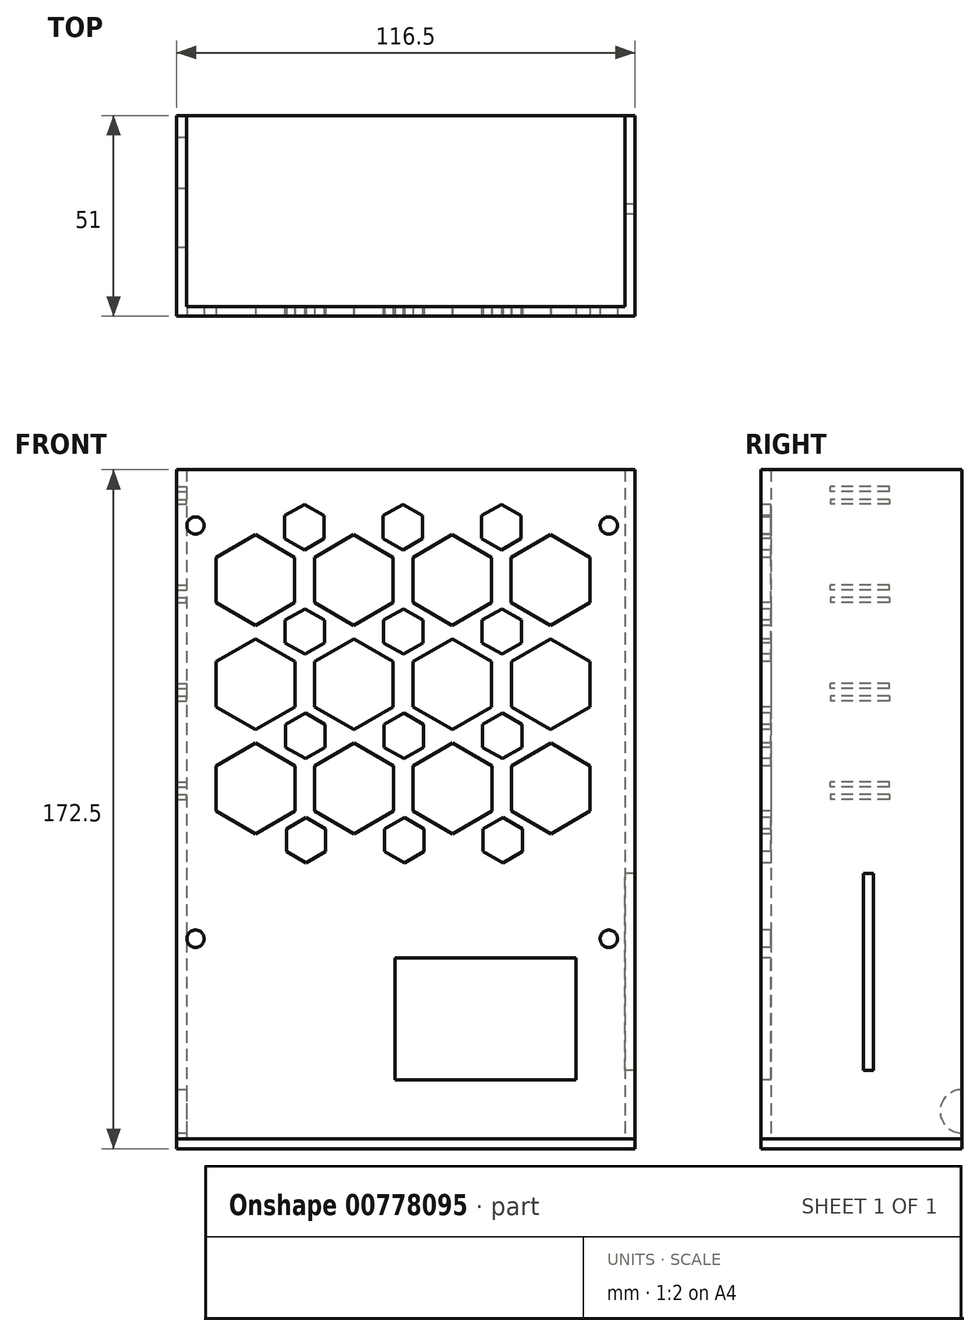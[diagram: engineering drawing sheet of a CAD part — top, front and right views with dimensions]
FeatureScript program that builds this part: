
annotation { "Feature Type Name" : "Feature", "Feature Type Description" : "" }
export const myFeature = defineFeature(function(context is Context, id is Id, definition is map)
    precondition{}
    {
        {
            var Q0;
            Q0=qCreatedBy(makeId("Top.planeOp"),FACE);
            var sketch = newSketch(context, id + "F0", { "sketchPlane" : qUnion([Q0])});
            skLineSegment(sketch, "E0", {"start": v(-38.54, 0) * mm, "end": v(77.96, 0) * mm});
            skLineSegment(sketch, "E1", {"start": v(-38.54, 0) * mm, "end": v(-38.54, 51) * mm});
            skLineSegment(sketch, "E2", {"start": v(77.96, 0) * mm, "end": v(77.96, 51) * mm});
            skLineSegment(sketch, "E3", {"start": v(-38.54, 51) * mm, "end": v(-36.04, 51) * mm});
            skLineSegment(sketch, "E4", {"start": v(-36.04, 51) * mm, "end": v(-36.04, 2.48) * mm});
            skLineSegment(sketch, "E5", {"start": v(-36.04, 2.48) * mm, "end": v(75.46, 2.48) * mm});
            skLineSegment(sketch, "E6", {"start": v(75.46, 2.48) * mm, "end": v(75.46, 51) * mm});
            skLineSegment(sketch, "E7", {"start": v(75.46, 51) * mm, "end": v(77.96, 51) * mm});
            skSolve(sketch);
        }
        {
            var Q0;
            Q0 = qSketchRegion(id + "F0", true);
            var Q1;
            Q1 = qSketchRegion(id + "F2", true);
            extrude(context, id + "F1", {"entities" : qUnion([Q0, Q1]), "depth" : 170 * mm, "offsetDistance" : 25.4 * mm});
        }
        {
            var Q0;
            Q0=qCreatedBy(makeId("Front.planeOp"),FACE);
            var sketch = newSketch(context, id + "F2", { "sketchPlane" : qUnion([Q0])});
            skLineSegment(sketch, "E8", {"start": v(-38.54, 0) * mm, "end": v(-38.54, -2.5) * mm});
            skLineSegment(sketch, "E9", {"start": v(-38.54, -2.5) * mm, "end": v(77.96, -2.5) * mm});
            skLineSegment(sketch, "E10", {"start": v(77.96, -2.5) * mm, "end": v(77.96, 0) * mm});
            skLineSegment(sketch, "E11", {"start": v(77.96, 0) * mm, "end": v(-38.54, 0) * mm});
            skSolve(sketch);
        }
        {
            var Q0;
            Q0 = qSketchRegion(id + "F2", true);
            extrude(context, id + "F3", {"entities" : qUnion([Q0]), "depth" : -51 * mm, "offsetDistance" : 25 * mm});
        }
        {
            var Q0;
            Q0=qCreatedBy(makeId("Front.planeOp"),FACE);
            var sketch = newSketch(context, id + "F4", { "sketchPlane" : qUnion([Q0])});
            skLineSegment(sketch, "E12.bottom", {"start": v(16.96, 46) * mm, "end": v(62.96, 46) * mm});
            skLineSegment(sketch, "E12.top", {"start": v(16.96, 15) * mm, "end": v(62.96, 15) * mm});
            skLineSegment(sketch, "E12.left", {"start": v(16.96, 46) * mm, "end": v(16.96, 15) * mm});
            skLineSegment(sketch, "E12.right", {"start": v(62.96, 46) * mm, "end": v(62.96, 15) * mm});
            skPoint(sketch, "E13", {"position": v(16.96, 0) * mm});
            skPoint(sketch, "E14", {"position": v(77.96, 15) * mm});
            skSolve(sketch);
        }
        {
            var Q0;
            Q0=makeQuery(id+"F4.imprint","IMPRINT",FACE,{"disambiguationData":[TD([[makeQuery(id+"F4.imprint","IMPRINT",EDGE,{"derivedFrom":sQuery(id+"F4.wireOp",EDGE,"E12.bottom")}),-1.0]])]});
            var Q1;
            Q1 = qSketchRegion(id + "F4", true);
            extrude(context, id + "F5", {"entities" : qUnion([Q0, Q1]), "operationType" : NewBodyOperationType.REMOVE, "depth" : -10 * mm, "offsetDistance" : 25 * mm});
        }
        {
            var Q0;
            Q0=qCreatedBy(makeId("Front.planeOp"),FACE);
            var sketch = newSketch(context, id + "F6", { "sketchPlane" : qUnion([Q0])});
            skLineSegment(sketch, "E15.left", {"start": v(-28.54, 180) * mm, "end": v(-28.54, 70) * mm});
            skLineSegment(sketch, "E15.right", {"start": v(67.96, 180) * mm, "end": v(67.96, 70) * mm});
            skCircle(sketch, "E16.1.0.0", {"center": v(31.5, 141.97) * mm, "radius": 11.55 * mm, "construction": true});
            skCircle(sketch, "E16.1.0.1", {"center": v(6.5, 141.97) * mm, "radius": 6.55 * mm, "construction": true});
            skLineSegment(sketch, "E16.1.0.2", {"start": v(50.83, 138.7) * mm, "end": v(50.83, 145.25) * mm});
            skLineSegment(sketch, "E16.1.0.3", {"start": v(-28.5, 136.2) * mm, "end": v(-28.5, 147.75) * mm});
            skLineSegment(sketch, "E16.1.0.4", {"start": v(-24.17, 138.7) * mm, "end": v(-24.17, 145.25) * mm});
            skLineSegment(sketch, "E16.1.0.5", {"start": v(-3.5, 136.2) * mm, "end": v(-3.5, 147.75) * mm});
            skLineSegment(sketch, "E16.1.0.6", {"start": v(46.5, 147.75) * mm, "end": v(56.5, 153.52) * mm});
            skLineSegment(sketch, "E16.1.0.7", {"start": v(16.5, 147.75) * mm, "end": v(16.5, 136.2) * mm});
            skLineSegment(sketch, "E16.1.0.8", {"start": v(12.17, 145.25) * mm, "end": v(12.17, 138.7) * mm});
            skLineSegment(sketch, "E16.1.0.9", {"start": v(31.5, 148.52) * mm, "end": v(37.17, 145.25) * mm});
            skLineSegment(sketch, "E16.1.0.10", {"start": v(6.5, 135.43) * mm, "end": v(0.83, 138.7) * mm});
            skLineSegment(sketch, "E16.1.0.11", {"start": v(66.5, 136.2) * mm, "end": v(56.5, 130.43) * mm});
            skLineSegment(sketch, "E16.1.0.12", {"start": v(56.5, 135.43) * mm, "end": v(50.83, 138.7) * mm});
            skCircle(sketch, "E16.1.0.13", {"center": v(31.5, 141.97) * mm, "radius": 6.55 * mm, "construction": true});
            skLineSegment(sketch, "E16.1.0.14", {"start": v(56.5, 153.52) * mm, "end": v(66.5, 147.75) * mm});
            skLineSegment(sketch, "E16.1.0.15", {"start": v(-18.5, 135.43) * mm, "end": v(-24.17, 138.7) * mm});
            skLineSegment(sketch, "E16.1.0.16", {"start": v(31.5, 130.43) * mm, "end": v(21.5, 136.2) * mm});
            skLineSegment(sketch, "E16.1.0.17", {"start": v(66.5, 147.75) * mm, "end": v(66.5, 136.2) * mm});
            skLineSegment(sketch, "E16.1.0.18", {"start": v(-18.5, 148.52) * mm, "end": v(-12.83, 145.25) * mm});
            skLineSegment(sketch, "E16.1.0.19", {"start": v(21.5, 147.75) * mm, "end": v(31.5, 153.52) * mm});
            skLineSegment(sketch, "E16.1.0.20", {"start": v(-24.17, 145.25) * mm, "end": v(-18.5, 148.52) * mm});
            skLineSegment(sketch, "E16.1.0.21", {"start": v(-18.5, 130.43) * mm, "end": v(-28.5, 136.2) * mm});
            skLineSegment(sketch, "E16.1.0.22", {"start": v(-18.5, 153.52) * mm, "end": v(-8.5, 147.75) * mm});
            skLineSegment(sketch, "E16.1.0.23", {"start": v(-28.5, 147.75) * mm, "end": v(-18.5, 153.52) * mm});
            skLineSegment(sketch, "E16.1.0.24", {"start": v(-12.83, 145.25) * mm, "end": v(-12.83, 138.7) * mm});
            skCircle(sketch, "E16.1.0.25", {"center": v(-18.5, 141.97) * mm, "radius": 6.55 * mm, "construction": true});
            skLineSegment(sketch, "E16.1.0.26", {"start": v(6.5, 130.43) * mm, "end": v(-3.5, 136.2) * mm});
            skLineSegment(sketch, "E16.1.0.27", {"start": v(25.83, 145.25) * mm, "end": v(31.5, 148.52) * mm});
            skLineSegment(sketch, "E16.1.0.28", {"start": v(56.5, 148.52) * mm, "end": v(62.17, 145.25) * mm});
            skCircle(sketch, "E16.1.0.29", {"center": v(-18.5, 141.97) * mm, "radius": 11.55 * mm, "construction": true});
            skLineSegment(sketch, "E16.1.0.30", {"start": v(6.5, 148.52) * mm, "end": v(12.17, 145.25) * mm});
            skLineSegment(sketch, "E16.1.0.31", {"start": v(41.5, 136.2) * mm, "end": v(31.5, 130.43) * mm});
            skLineSegment(sketch, "E16.1.0.32", {"start": v(46.5, 136.2) * mm, "end": v(46.5, 147.75) * mm});
            skLineSegment(sketch, "E16.1.0.33", {"start": v(-8.5, 136.2) * mm, "end": v(-18.5, 130.43) * mm});
            skLineSegment(sketch, "E16.1.0.34", {"start": v(-8.5, 147.75) * mm, "end": v(-8.5, 136.2) * mm});
            skLineSegment(sketch, "E16.1.0.35", {"start": v(62.17, 145.25) * mm, "end": v(62.17, 138.7) * mm});
            skLineSegment(sketch, "E16.1.0.36", {"start": v(37.17, 138.7) * mm, "end": v(31.5, 135.43) * mm});
            skLineSegment(sketch, "E16.1.0.37", {"start": v(0.83, 138.7) * mm, "end": v(0.83, 145.25) * mm});
            skLineSegment(sketch, "E16.1.0.38", {"start": v(16.5, 136.2) * mm, "end": v(6.5, 130.43) * mm});
            skLineSegment(sketch, "E16.1.0.39", {"start": v(37.17, 145.25) * mm, "end": v(37.17, 138.7) * mm});
            skLineSegment(sketch, "E16.1.0.40", {"start": v(56.5, 130.43) * mm, "end": v(46.5, 136.2) * mm});
            skLineSegment(sketch, "E16.1.0.41", {"start": v(-28.5, 136.2) * mm, "end": v(-3.5, 136.2) * mm, "construction": true});
            skLineSegment(sketch, "E16.1.0.42", {"start": v(12.17, 138.7) * mm, "end": v(6.5, 135.43) * mm});
            skLineSegment(sketch, "E16.1.0.43", {"start": v(31.5, 135.43) * mm, "end": v(25.83, 138.7) * mm});
            skCircle(sketch, "E16.1.0.44", {"center": v(56.5, 141.97) * mm, "radius": 6.55 * mm, "construction": true});
            skLineSegment(sketch, "E16.1.0.45", {"start": v(50.83, 145.25) * mm, "end": v(56.5, 148.52) * mm});
            skLineSegment(sketch, "E16.1.0.46", {"start": v(31.5, 153.52) * mm, "end": v(41.5, 147.75) * mm});
            skLineSegment(sketch, "E16.1.0.47", {"start": v(21.5, 136.2) * mm, "end": v(21.5, 147.75) * mm});
            skCircle(sketch, "E16.1.0.48", {"center": v(56.5, 141.97) * mm, "radius": 11.55 * mm, "construction": true});
            skLineSegment(sketch, "E16.1.0.49", {"start": v(-3.5, 147.75) * mm, "end": v(6.5, 153.52) * mm});
            skLineSegment(sketch, "E16.1.0.50", {"start": v(25.83, 138.7) * mm, "end": v(25.83, 145.25) * mm});
            skLineSegment(sketch, "E16.1.0.51", {"start": v(62.17, 138.7) * mm, "end": v(56.5, 135.43) * mm});
            skCircle(sketch, "E16.1.0.52", {"center": v(6.5, 141.97) * mm, "radius": 11.55 * mm, "construction": true});
            skLineSegment(sketch, "E16.1.0.53", {"start": v(41.5, 147.75) * mm, "end": v(41.5, 136.2) * mm});
            skLineSegment(sketch, "E16.1.0.54", {"start": v(0.83, 145.25) * mm, "end": v(6.5, 148.52) * mm});
            skLineSegment(sketch, "E16.1.0.55", {"start": v(6.5, 153.52) * mm, "end": v(16.5, 147.75) * mm});
            skLineSegment(sketch, "E16.1.0.56", {"start": v(-12.83, 138.7) * mm, "end": v(-18.5, 135.43) * mm});
            skCircle(sketch, "E16.2.0.0", {"center": v(31.54, 115.5) * mm, "radius": 11.55 * mm, "construction": true});
            skCircle(sketch, "E16.2.0.1", {"center": v(6.54, 115.5) * mm, "radius": 6.55 * mm, "construction": true});
            skLineSegment(sketch, "E16.2.0.2", {"start": v(50.87, 112.22) * mm, "end": v(50.87, 118.77) * mm});
            skLineSegment(sketch, "E16.2.0.3", {"start": v(-28.46, 109.72) * mm, "end": v(-28.46, 121.27) * mm});
            skLineSegment(sketch, "E16.2.0.4", {"start": v(-24.13, 112.22) * mm, "end": v(-24.13, 118.77) * mm});
            skLineSegment(sketch, "E16.2.0.5", {"start": v(-3.46, 109.72) * mm, "end": v(-3.46, 121.27) * mm});
            skLineSegment(sketch, "E16.2.0.6", {"start": v(46.54, 121.27) * mm, "end": v(56.54, 127.04) * mm});
            skLineSegment(sketch, "E16.2.0.7", {"start": v(16.54, 121.27) * mm, "end": v(16.54, 109.72) * mm});
            skLineSegment(sketch, "E16.2.0.8", {"start": v(12.2, 118.77) * mm, "end": v(12.2, 112.22) * mm});
            skLineSegment(sketch, "E16.2.0.9", {"start": v(31.54, 122.04) * mm, "end": v(37.2, 118.77) * mm});
            skLineSegment(sketch, "E16.2.0.10", {"start": v(6.54, 108.95) * mm, "end": v(0.87, 112.22) * mm});
            skLineSegment(sketch, "E16.2.0.11", {"start": v(66.54, 109.72) * mm, "end": v(56.54, 103.95) * mm});
            skLineSegment(sketch, "E16.2.0.12", {"start": v(56.54, 108.95) * mm, "end": v(50.87, 112.22) * mm});
            skCircle(sketch, "E16.2.0.13", {"center": v(31.54, 115.5) * mm, "radius": 6.55 * mm, "construction": true});
            skLineSegment(sketch, "E16.2.0.14", {"start": v(56.54, 127.04) * mm, "end": v(66.54, 121.27) * mm});
            skLineSegment(sketch, "E16.2.0.15", {"start": v(-18.46, 108.95) * mm, "end": v(-24.13, 112.22) * mm});
            skLineSegment(sketch, "E16.2.0.16", {"start": v(31.54, 103.95) * mm, "end": v(21.54, 109.72) * mm});
            skLineSegment(sketch, "E16.2.0.17", {"start": v(66.54, 121.27) * mm, "end": v(66.54, 109.72) * mm});
            skLineSegment(sketch, "E16.2.0.18", {"start": v(-18.46, 122.04) * mm, "end": v(-12.8, 118.77) * mm});
            skLineSegment(sketch, "E16.2.0.19", {"start": v(21.54, 121.27) * mm, "end": v(31.54, 127.04) * mm});
            skLineSegment(sketch, "E16.2.0.20", {"start": v(-24.13, 118.77) * mm, "end": v(-18.46, 122.04) * mm});
            skLineSegment(sketch, "E16.2.0.21", {"start": v(-18.46, 103.95) * mm, "end": v(-28.46, 109.72) * mm});
            skLineSegment(sketch, "E16.2.0.22", {"start": v(-18.46, 127.04) * mm, "end": v(-8.46, 121.27) * mm});
            skLineSegment(sketch, "E16.2.0.23", {"start": v(-28.46, 121.27) * mm, "end": v(-18.46, 127.04) * mm});
            skLineSegment(sketch, "E16.2.0.24", {"start": v(-12.8, 118.77) * mm, "end": v(-12.8, 112.22) * mm});
            skCircle(sketch, "E16.2.0.25", {"center": v(-18.46, 115.5) * mm, "radius": 6.55 * mm, "construction": true});
            skLineSegment(sketch, "E16.2.0.26", {"start": v(6.54, 103.95) * mm, "end": v(-3.46, 109.72) * mm});
            skLineSegment(sketch, "E16.2.0.27", {"start": v(25.87, 118.77) * mm, "end": v(31.54, 122.04) * mm});
            skLineSegment(sketch, "E16.2.0.28", {"start": v(56.54, 122.04) * mm, "end": v(62.2, 118.77) * mm});
            skCircle(sketch, "E16.2.0.29", {"center": v(-18.46, 115.5) * mm, "radius": 11.55 * mm, "construction": true});
            skLineSegment(sketch, "E16.2.0.30", {"start": v(6.54, 122.04) * mm, "end": v(12.2, 118.77) * mm});
            skLineSegment(sketch, "E16.2.0.31", {"start": v(41.54, 109.72) * mm, "end": v(31.54, 103.95) * mm});
            skLineSegment(sketch, "E16.2.0.32", {"start": v(46.54, 109.72) * mm, "end": v(46.54, 121.27) * mm});
            skLineSegment(sketch, "E16.2.0.33", {"start": v(-8.46, 109.72) * mm, "end": v(-18.46, 103.95) * mm});
            skLineSegment(sketch, "E16.2.0.34", {"start": v(-8.46, 121.27) * mm, "end": v(-8.46, 109.72) * mm});
            skLineSegment(sketch, "E16.2.0.35", {"start": v(62.2, 118.77) * mm, "end": v(62.2, 112.22) * mm});
            skLineSegment(sketch, "E16.2.0.36", {"start": v(37.2, 112.22) * mm, "end": v(31.54, 108.95) * mm});
            skLineSegment(sketch, "E16.2.0.37", {"start": v(0.87, 112.22) * mm, "end": v(0.87, 118.77) * mm});
            skLineSegment(sketch, "E16.2.0.38", {"start": v(16.54, 109.72) * mm, "end": v(6.54, 103.95) * mm});
            skLineSegment(sketch, "E16.2.0.39", {"start": v(37.2, 118.77) * mm, "end": v(37.2, 112.22) * mm});
            skLineSegment(sketch, "E16.2.0.40", {"start": v(56.54, 103.95) * mm, "end": v(46.54, 109.72) * mm});
            skLineSegment(sketch, "E16.2.0.41", {"start": v(-28.46, 109.72) * mm, "end": v(-3.46, 109.72) * mm, "construction": true});
            skLineSegment(sketch, "E16.2.0.42", {"start": v(12.2, 112.22) * mm, "end": v(6.54, 108.95) * mm});
            skLineSegment(sketch, "E16.2.0.43", {"start": v(31.54, 108.95) * mm, "end": v(25.87, 112.22) * mm});
            skCircle(sketch, "E16.2.0.44", {"center": v(56.54, 115.5) * mm, "radius": 6.55 * mm, "construction": true});
            skLineSegment(sketch, "E16.2.0.45", {"start": v(50.87, 118.77) * mm, "end": v(56.54, 122.04) * mm});
            skLineSegment(sketch, "E16.2.0.46", {"start": v(31.54, 127.04) * mm, "end": v(41.54, 121.27) * mm});
            skLineSegment(sketch, "E16.2.0.47", {"start": v(21.54, 109.72) * mm, "end": v(21.54, 121.27) * mm});
            skCircle(sketch, "E16.2.0.48", {"center": v(56.54, 115.5) * mm, "radius": 11.55 * mm, "construction": true});
            skLineSegment(sketch, "E16.2.0.49", {"start": v(-3.46, 121.27) * mm, "end": v(6.54, 127.04) * mm});
            skLineSegment(sketch, "E16.2.0.50", {"start": v(25.87, 112.22) * mm, "end": v(25.87, 118.77) * mm});
            skLineSegment(sketch, "E16.2.0.51", {"start": v(62.2, 112.22) * mm, "end": v(56.54, 108.95) * mm});
            skCircle(sketch, "E16.2.0.52", {"center": v(6.54, 115.5) * mm, "radius": 11.55 * mm, "construction": true});
            skLineSegment(sketch, "E16.2.0.53", {"start": v(41.54, 121.27) * mm, "end": v(41.54, 109.72) * mm});
            skLineSegment(sketch, "E16.2.0.54", {"start": v(0.87, 118.77) * mm, "end": v(6.54, 122.04) * mm});
            skLineSegment(sketch, "E16.2.0.55", {"start": v(6.54, 127.04) * mm, "end": v(16.54, 121.27) * mm});
            skLineSegment(sketch, "E16.2.0.56", {"start": v(-12.8, 112.22) * mm, "end": v(-18.46, 108.95) * mm});
            skCircle(sketch, "E16.3.0.0", {"center": v(31.57, 89.01) * mm, "radius": 11.55 * mm, "construction": true});
            skCircle(sketch, "E16.3.0.1", {"center": v(6.57, 89.01) * mm, "radius": 6.55 * mm, "construction": true});
            skLineSegment(sketch, "E16.3.0.2", {"start": v(50.9, 85.74) * mm, "end": v(50.9, 92.29) * mm});
            skLineSegment(sketch, "E16.3.0.3", {"start": v(-28.43, 83.24) * mm, "end": v(-28.43, 94.79) * mm});
            skLineSegment(sketch, "E16.3.0.4", {"start": v(-24.1, 85.74) * mm, "end": v(-24.1, 92.29) * mm});
            skLineSegment(sketch, "E16.3.0.5", {"start": v(-3.43, 83.24) * mm, "end": v(-3.43, 94.79) * mm});
            skLineSegment(sketch, "E16.3.0.6", {"start": v(46.57, 94.79) * mm, "end": v(56.57, 100.56) * mm});
            skLineSegment(sketch, "E16.3.0.7", {"start": v(16.57, 94.79) * mm, "end": v(16.57, 83.24) * mm});
            skLineSegment(sketch, "E16.3.0.8", {"start": v(12.24, 92.29) * mm, "end": v(12.24, 85.74) * mm});
            skLineSegment(sketch, "E16.3.0.9", {"start": v(31.57, 95.56) * mm, "end": v(37.24, 92.29) * mm});
            skLineSegment(sketch, "E16.3.0.10", {"start": v(6.57, 82.47) * mm, "end": v(0.9, 85.74) * mm});
            skLineSegment(sketch, "E16.3.0.11", {"start": v(66.57, 83.24) * mm, "end": v(56.57, 77.47) * mm});
            skLineSegment(sketch, "E16.3.0.12", {"start": v(56.57, 82.47) * mm, "end": v(50.9, 85.74) * mm});
            skCircle(sketch, "E16.3.0.13", {"center": v(31.57, 89.01) * mm, "radius": 6.55 * mm, "construction": true});
            skLineSegment(sketch, "E16.3.0.14", {"start": v(56.57, 100.56) * mm, "end": v(66.57, 94.79) * mm});
            skLineSegment(sketch, "E16.3.0.15", {"start": v(-18.43, 82.47) * mm, "end": v(-24.1, 85.74) * mm});
            skLineSegment(sketch, "E16.3.0.16", {"start": v(31.57, 77.47) * mm, "end": v(21.57, 83.24) * mm});
            skLineSegment(sketch, "E16.3.0.17", {"start": v(66.57, 94.79) * mm, "end": v(66.57, 83.24) * mm});
            skLineSegment(sketch, "E16.3.0.18", {"start": v(-18.43, 95.56) * mm, "end": v(-12.76, 92.29) * mm});
            skLineSegment(sketch, "E16.3.0.19", {"start": v(21.57, 94.79) * mm, "end": v(31.57, 100.56) * mm});
            skLineSegment(sketch, "E16.3.0.20", {"start": v(-24.1, 92.29) * mm, "end": v(-18.43, 95.56) * mm});
            skLineSegment(sketch, "E16.3.0.21", {"start": v(-18.43, 77.47) * mm, "end": v(-28.43, 83.24) * mm});
            skLineSegment(sketch, "E16.3.0.22", {"start": v(-18.43, 100.56) * mm, "end": v(-8.43, 94.79) * mm});
            skLineSegment(sketch, "E16.3.0.23", {"start": v(-28.43, 94.79) * mm, "end": v(-18.43, 100.56) * mm});
            skLineSegment(sketch, "E16.3.0.24", {"start": v(-12.76, 92.29) * mm, "end": v(-12.76, 85.74) * mm});
            skCircle(sketch, "E16.3.0.25", {"center": v(-18.43, 89.01) * mm, "radius": 6.55 * mm, "construction": true});
            skLineSegment(sketch, "E16.3.0.26", {"start": v(6.57, 77.47) * mm, "end": v(-3.43, 83.24) * mm});
            skLineSegment(sketch, "E16.3.0.27", {"start": v(25.9, 92.29) * mm, "end": v(31.57, 95.56) * mm});
            skLineSegment(sketch, "E16.3.0.28", {"start": v(56.57, 95.56) * mm, "end": v(62.24, 92.29) * mm});
            skCircle(sketch, "E16.3.0.29", {"center": v(-18.43, 89.01) * mm, "radius": 11.55 * mm, "construction": true});
            skLineSegment(sketch, "E16.3.0.30", {"start": v(6.57, 95.56) * mm, "end": v(12.24, 92.29) * mm});
            skLineSegment(sketch, "E16.3.0.31", {"start": v(41.57, 83.24) * mm, "end": v(31.57, 77.47) * mm});
            skLineSegment(sketch, "E16.3.0.32", {"start": v(46.57, 83.24) * mm, "end": v(46.57, 94.79) * mm});
            skLineSegment(sketch, "E16.3.0.33", {"start": v(-8.43, 83.24) * mm, "end": v(-18.43, 77.47) * mm});
            skLineSegment(sketch, "E16.3.0.34", {"start": v(-8.43, 94.79) * mm, "end": v(-8.43, 83.24) * mm});
            skLineSegment(sketch, "E16.3.0.35", {"start": v(62.24, 92.29) * mm, "end": v(62.24, 85.74) * mm});
            skLineSegment(sketch, "E16.3.0.36", {"start": v(37.24, 85.74) * mm, "end": v(31.57, 82.47) * mm});
            skLineSegment(sketch, "E16.3.0.37", {"start": v(0.9, 85.74) * mm, "end": v(0.9, 92.29) * mm});
            skLineSegment(sketch, "E16.3.0.38", {"start": v(16.57, 83.24) * mm, "end": v(6.57, 77.47) * mm});
            skLineSegment(sketch, "E16.3.0.39", {"start": v(37.24, 92.29) * mm, "end": v(37.24, 85.74) * mm});
            skLineSegment(sketch, "E16.3.0.40", {"start": v(56.57, 77.47) * mm, "end": v(46.57, 83.24) * mm});
            skLineSegment(sketch, "E16.3.0.41", {"start": v(-28.43, 83.24) * mm, "end": v(-3.43, 83.24) * mm, "construction": true});
            skLineSegment(sketch, "E16.3.0.42", {"start": v(12.24, 85.74) * mm, "end": v(6.57, 82.47) * mm});
            skLineSegment(sketch, "E16.3.0.43", {"start": v(31.57, 82.47) * mm, "end": v(25.9, 85.74) * mm});
            skCircle(sketch, "E16.3.0.44", {"center": v(56.57, 89.01) * mm, "radius": 6.55 * mm, "construction": true});
            skLineSegment(sketch, "E16.3.0.45", {"start": v(50.9, 92.29) * mm, "end": v(56.57, 95.56) * mm});
            skLineSegment(sketch, "E16.3.0.46", {"start": v(31.57, 100.56) * mm, "end": v(41.57, 94.79) * mm});
            skLineSegment(sketch, "E16.3.0.47", {"start": v(21.57, 83.24) * mm, "end": v(21.57, 94.79) * mm});
            skCircle(sketch, "E16.3.0.48", {"center": v(56.57, 89.01) * mm, "radius": 11.55 * mm, "construction": true});
            skLineSegment(sketch, "E16.3.0.49", {"start": v(-3.43, 94.79) * mm, "end": v(6.57, 100.56) * mm});
            skLineSegment(sketch, "E16.3.0.50", {"start": v(25.9, 85.74) * mm, "end": v(25.9, 92.29) * mm});
            skLineSegment(sketch, "E16.3.0.51", {"start": v(62.24, 85.74) * mm, "end": v(56.57, 82.47) * mm});
            skCircle(sketch, "E16.3.0.52", {"center": v(6.57, 89.01) * mm, "radius": 11.55 * mm, "construction": true});
            skLineSegment(sketch, "E16.3.0.53", {"start": v(41.57, 94.79) * mm, "end": v(41.57, 83.24) * mm});
            skLineSegment(sketch, "E16.3.0.54", {"start": v(0.9, 92.29) * mm, "end": v(6.57, 95.56) * mm});
            skLineSegment(sketch, "E16.3.0.55", {"start": v(6.57, 100.56) * mm, "end": v(16.57, 94.79) * mm});
            skLineSegment(sketch, "E16.3.0.56", {"start": v(-12.76, 85.74) * mm, "end": v(-18.43, 82.47) * mm});
            skLineSegment(sketch, "E16.direction1", {"start": v(-28.54, 162.68) * mm, "end": v(-28.5, 136.2) * mm, "construction": true});
            skSolve(sketch);
        }
        {
            var Q0;
            Q0=makeQuery(id+"F6.imprint","IMPRINT",FACE,{"disambiguationData":[TD([[makeQuery(id+"F6.imprint","IMPRINT",EDGE,{"derivedFrom":sQuery(id+"F6.wireOp",EDGE,"4cea52ef-489a-4c24-b989-f0e8c5ddf205.0")}),-1.0]])]});
            var Q1;
            Q1=makeQuery(id+"F6.imprint","IMPRINT",FACE,{"disambiguationData":[TD([[makeQuery(id+"F6.imprint","IMPRINT",EDGE,{"derivedFrom":sQuery(id+"F6.wireOp",EDGE,"bbeef76b-191c-468b-84a6-78bb34565442.1.0.2")}),-1.0]])]});
            var Q2;
            Q2=makeQuery(id+"F6.imprint","IMPRINT",FACE,{"disambiguationData":[TD([[makeQuery(id+"F6.imprint","IMPRINT",EDGE,{"derivedFrom":sQuery(id+"F6.wireOp",EDGE,"bbeef76b-191c-468b-84a6-78bb34565442.2.0.2")}),-1.0]])]});
            var Q3;
            Q3=makeQuery(id+"F6.imprint","IMPRINT",FACE,{"disambiguationData":[TD([[makeQuery(id+"F6.imprint","IMPRINT",EDGE,{"derivedFrom":sQuery(id+"F6.wireOp",EDGE,"bbeef76b-191c-468b-84a6-78bb34565442.3.0.2")}),-1.0]])]});
            var Q4;
            Q4=makeQuery(id+"F6.imprint","IMPRINT",FACE,{"disambiguationData":[TD([[makeQuery(id+"F6.imprint","IMPRINT",EDGE,{"derivedFrom":sQuery(id+"F6.wireOp",EDGE,"E16.1.0.2")}),-1.0]])]});
            var Q5;
            Q5=makeQuery(id+"F6.imprint","IMPRINT",FACE,{"disambiguationData":[TD([[makeQuery(id+"F6.imprint","IMPRINT",EDGE,{"derivedFrom":sQuery(id+"F6.wireOp",EDGE,"E16.1.0.9")}),-1.0]])]});
            var Q6;
            Q6=makeQuery(id+"F6.imprint","IMPRINT",FACE,{"disambiguationData":[TD([[makeQuery(id+"F6.imprint","IMPRINT",EDGE,{"derivedFrom":sQuery(id+"F6.wireOp",EDGE,"E16.1.0.8")}),-1.0]])]});
            var Q7;
            Q7=makeQuery(id+"F6.imprint","IMPRINT",FACE,{"disambiguationData":[TD([[makeQuery(id+"F6.imprint","IMPRINT",EDGE,{"derivedFrom":sQuery(id+"F6.wireOp",EDGE,"E16.1.0.4")}),-1.0]])]});
            var Q8;
            Q8=makeQuery(id+"F6.imprint","IMPRINT",FACE,{"disambiguationData":[TD([[makeQuery(id+"F6.imprint","IMPRINT",EDGE,{"derivedFrom":sQuery(id+"F6.wireOp",EDGE,"E16.2.0.4")}),-1.0]])]});
            var Q9;
            Q9=makeQuery(id+"F6.imprint","IMPRINT",FACE,{"disambiguationData":[TD([[makeQuery(id+"F6.imprint","IMPRINT",EDGE,{"derivedFrom":sQuery(id+"F6.wireOp",EDGE,"E16.2.0.8")}),-1.0]])]});
            var Q10;
            Q10=makeQuery(id+"F6.imprint","IMPRINT",FACE,{"disambiguationData":[TD([[makeQuery(id+"F6.imprint","IMPRINT",EDGE,{"derivedFrom":sQuery(id+"F6.wireOp",EDGE,"E16.2.0.9")}),-1.0]])]});
            var Q11;
            Q11=makeQuery(id+"F6.imprint","IMPRINT",FACE,{"disambiguationData":[TD([[makeQuery(id+"F6.imprint","IMPRINT",EDGE,{"derivedFrom":sQuery(id+"F6.wireOp",EDGE,"E16.2.0.2")}),-1.0]])]});
            var Q12;
            Q12=makeQuery(id+"F6.imprint","IMPRINT",FACE,{"disambiguationData":[TD([[makeQuery(id+"F6.imprint","IMPRINT",EDGE,{"derivedFrom":sQuery(id+"F6.wireOp",EDGE,"E16.3.0.2")}),-1.0]])]});
            var Q13;
            Q13=makeQuery(id+"F6.imprint","IMPRINT",FACE,{"disambiguationData":[TD([[makeQuery(id+"F6.imprint","IMPRINT",EDGE,{"derivedFrom":sQuery(id+"F6.wireOp",EDGE,"E16.3.0.9")}),-1.0]])]});
            var Q14;
            Q14=makeQuery(id+"F6.imprint","IMPRINT",FACE,{"disambiguationData":[TD([[makeQuery(id+"F6.imprint","IMPRINT",EDGE,{"derivedFrom":sQuery(id+"F6.wireOp",EDGE,"E16.3.0.8")}),-1.0]])]});
            var Q15;
            Q15=makeQuery(id+"F6.imprint","IMPRINT",FACE,{"disambiguationData":[TD([[makeQuery(id+"F6.imprint","IMPRINT",EDGE,{"derivedFrom":sQuery(id+"F6.wireOp",EDGE,"E16.3.0.4")}),-1.0]])]});
            var Q16;
            {var subQ4=sQuery(id+"F6.wireOp",EDGE,"E16.4.0.18");Q16=makeQuery(id+"F6.imprint","IMPRINT",FACE,{"disambiguationData":[TD([[makeQuery(id+"F6.imprint","IMPRINT",EDGE,{"derivedFrom":subQ4}),-1.0]])]});}
            var Q17;
            {var subQ4=sQuery(id+"F6.wireOp",EDGE,"E16.4.0.15");Q17=makeQuery(id+"F6.imprint","IMPRINT",FACE,{"disambiguationData":[TD([[makeQuery(id+"F6.imprint","IMPRINT",EDGE,{"derivedFrom":subQ4}),-1.0]])]});}
            var Q18;
            {var subQ1=sQuery(id+"F6.wireOp",EDGE,"E16.4.0.10");Q18=makeQuery(id+"F6.imprint","IMPRINT",FACE,{"disambiguationData":[TD([[makeQuery(id+"F6.imprint","IMPRINT",EDGE,{"derivedFrom":subQ1}),-1.0]])]});}
            var Q19;
            {var subQ4=sQuery(id+"F6.wireOp",EDGE,"E16.4.0.30");Q19=makeQuery(id+"F6.imprint","IMPRINT",FACE,{"disambiguationData":[TD([[makeQuery(id+"F6.imprint","IMPRINT",EDGE,{"derivedFrom":subQ4}),-1.0]])]});}
            var Q20;
            {var subQ1=sQuery(id+"F6.wireOp",EDGE,"E16.4.0.9");Q20=makeQuery(id+"F6.imprint","IMPRINT",FACE,{"disambiguationData":[TD([[makeQuery(id+"F6.imprint","IMPRINT",EDGE,{"derivedFrom":subQ1}),-1.0]])]});}
            var Q21;
            {var subQ1=sQuery(id+"F6.wireOp",EDGE,"E16.4.0.36");Q21=makeQuery(id+"F6.imprint","IMPRINT",FACE,{"disambiguationData":[TD([[makeQuery(id+"F6.imprint","IMPRINT",EDGE,{"derivedFrom":subQ1}),-1.0]])]});}
            var Q22;
            {var subQ1=sQuery(id+"F6.wireOp",EDGE,"E16.4.0.28");Q22=makeQuery(id+"F6.imprint","IMPRINT",FACE,{"disambiguationData":[TD([[makeQuery(id+"F6.imprint","IMPRINT",EDGE,{"derivedFrom":subQ1}),-1.0]])]});}
            var Q23;
            {var subQ4=sQuery(id+"F6.wireOp",EDGE,"E16.4.0.12");Q23=makeQuery(id+"F6.imprint","IMPRINT",FACE,{"disambiguationData":[TD([[makeQuery(id+"F6.imprint","IMPRINT",EDGE,{"derivedFrom":subQ4}),-1.0]])]});}
            var Q24;
            Q24=makeQuery(id+"F6.imprint","IMPRINT",FACE,{"disambiguationData":[TD([[makeQuery(id+"F6.imprint","IMPRINT",EDGE,{"derivedFrom":sQuery(id+"F6.wireOp",EDGE,"bbeef76b-191c-468b-84a6-78bb34565442.3.0.0")}),-1.0]])]});
            var Q25;
            Q25=makeQuery(id+"F6.imprint","IMPRINT",FACE,{"disambiguationData":[TD([[makeQuery(id+"F6.imprint","IMPRINT",EDGE,{"derivedFrom":sQuery(id+"F6.wireOp",EDGE,"E16.1.0.9")}),1.0]])]});
            var Q26;
            Q26=makeQuery(id+"F6.imprint","IMPRINT",FACE,{"disambiguationData":[TD([[makeQuery(id+"F6.imprint","IMPRINT",EDGE,{"derivedFrom":sQuery(id+"F6.wireOp",EDGE,"bbeef76b-191c-468b-84a6-78bb34565442.1.0.0")}),-1.0]])]});
            var Q27;
            Q27=makeQuery(id+"F6.imprint","IMPRINT",FACE,{"disambiguationData":[TD([[makeQuery(id+"F6.imprint","IMPRINT",EDGE,{"derivedFrom":sQuery(id+"F6.wireOp",EDGE,"E16.2.0.2")}),1.0]])]});
            var Q28;
            Q28=makeQuery(id+"F6.imprint","IMPRINT",FACE,{"disambiguationData":[TD([[makeQuery(id+"F6.imprint","IMPRINT",EDGE,{"derivedFrom":sQuery(id+"F6.wireOp",EDGE,"E16.2.0.5")}),-1.0]])]});
            var Q29;
            Q29=makeQuery(id+"F6.imprint","IMPRINT",FACE,{"disambiguationData":[TD([[makeQuery(id+"F6.imprint","IMPRINT",EDGE,{"derivedFrom":sQuery(id+"F6.wireOp",EDGE,"E16.3.0.9")}),1.0]])]});
            var Q30;
            {var subQ13=sQuery(id+"F6.wireOp",EDGE,"E16.4.0.6");Q30=makeQuery(id+"F6.imprint","IMPRINT",FACE,{"disambiguationData":[TD([[makeQuery(id+"F6.imprint","IMPRINT",EDGE,{"derivedFrom":subQ13}),-1.0]])]});}
            var Q31;
            {var subQ11=sQuery(id+"F6.wireOp",EDGE,"E16.4.0.30");Q31=makeQuery(id+"F6.imprint","IMPRINT",FACE,{"disambiguationData":[TD([[makeQuery(id+"F6.imprint","IMPRINT",EDGE,{"derivedFrom":subQ11}),1.0]])]});}
            var Q32;
            {var subQ10=sQuery(id+"F6.wireOp",EDGE,"E16.4.0.10");Q32=makeQuery(id+"F6.imprint","IMPRINT",FACE,{"disambiguationData":[TD([[makeQuery(id+"F6.imprint","IMPRINT",EDGE,{"derivedFrom":subQ10}),1.0]])]});}
            var Q33;
            Q33=makeQuery(id+"F6.imprint","IMPRINT",FACE,{"disambiguationData":[TD([[makeQuery(id+"F6.imprint","IMPRINT",EDGE,{"derivedFrom":sQuery(id+"F6.wireOp",EDGE,"E16.4.0.11")}),-1.0]])]});
            var Q34;
            Q34=makeQuery(id+"F6.imprint","IMPRINT",FACE,{"disambiguationData":[TD([[makeQuery(id+"F6.imprint","IMPRINT",EDGE,{"derivedFrom":sQuery(id+"F6.wireOp",EDGE,"E16.2.0.9")}),1.0]])]});
            var Q35;
            Q35=makeQuery(id+"F6.imprint","IMPRINT",FACE,{"disambiguationData":[TD([[makeQuery(id+"F6.imprint","IMPRINT",EDGE,{"derivedFrom":sQuery(id+"F6.wireOp",EDGE,"bbeef76b-191c-468b-84a6-78bb34565442.2.0.0")}),-1.0]])]});
            var Q36;
            Q36=makeQuery(id+"F6.imprint","IMPRINT",FACE,{"disambiguationData":[TD([[makeQuery(id+"F6.imprint","IMPRINT",EDGE,{"derivedFrom":sQuery(id+"F6.wireOp",EDGE,"c7429df2-12dd-4cba-ae4a-5a3fa0d102de.0")}),-1.0]])]});
            var Q37;
            Q37=makeQuery(id+"F6.imprint","IMPRINT",FACE,{"disambiguationData":[TD([[makeQuery(id+"F6.imprint","IMPRINT",EDGE,{"derivedFrom":sQuery(id+"F6.wireOp",EDGE,"E16.1.0.3")}),-1.0]])]});
            var Q38;
            Q38=makeQuery(id+"F6.imprint","IMPRINT",FACE,{"disambiguationData":[TD([[makeQuery(id+"F6.imprint","IMPRINT",EDGE,{"derivedFrom":sQuery(id+"F6.wireOp",EDGE,"E16.2.0.3")}),-1.0]])]});
            var Q39;
            Q39=makeQuery(id+"F6.imprint","IMPRINT",FACE,{"disambiguationData":[TD([[makeQuery(id+"F6.imprint","IMPRINT",EDGE,{"derivedFrom":sQuery(id+"F6.wireOp",EDGE,"E16.3.0.3")}),-1.0]])]});
            var Q40;
            {var subQ12=sQuery(id+"F6.wireOp",EDGE,"E16.4.0.18");Q40=makeQuery(id+"F6.imprint","IMPRINT",FACE,{"disambiguationData":[TD([[makeQuery(id+"F6.imprint","IMPRINT",EDGE,{"derivedFrom":subQ12}),1.0]])]});}
            var Q41;
            {var subQ0=sQuery(id+"F6.wireOp",EDGE,"E16.4.0.15");Q41=makeQuery(id+"F6.imprint","IMPRINT",FACE,{"disambiguationData":[TD([[makeQuery(id+"F6.imprint","IMPRINT",EDGE,{"derivedFrom":subQ0}),1.0]])]});}
            var Q42;
            Q42=makeQuery(id+"F6.imprint","IMPRINT",FACE,{"disambiguationData":[TD([[makeQuery(id+"F6.imprint","IMPRINT",EDGE,{"derivedFrom":sQuery(id+"F6.wireOp",EDGE,"E16.3.0.5")}),-1.0]])]});
            var Q43;
            {var subQ1=sQuery(id+"F6.wireOp",EDGE,"E16.4.0.9");Q43=makeQuery(id+"F6.imprint","IMPRINT",FACE,{"disambiguationData":[TD([[makeQuery(id+"F6.imprint","IMPRINT",EDGE,{"derivedFrom":subQ1}),1.0]])]});}
            var Q44;
            {var subQ0=sQuery(id+"F6.wireOp",EDGE,"E16.4.0.16");Q44=makeQuery(id+"F6.imprint","IMPRINT",FACE,{"disambiguationData":[TD([[makeQuery(id+"F6.imprint","IMPRINT",EDGE,{"derivedFrom":subQ0}),-1.0]])]});}
            var Q45;
            Q45=makeQuery(id+"F6.imprint","IMPRINT",FACE,{"disambiguationData":[TD([[makeQuery(id+"F6.imprint","IMPRINT",EDGE,{"derivedFrom":sQuery(id+"F6.wireOp",EDGE,"E16.3.0.2")}),1.0]])]});
            var Q46;
            Q46=makeQuery(id+"F6.imprint","IMPRINT",FACE,{"disambiguationData":[TD([[makeQuery(id+"F6.imprint","IMPRINT",EDGE,{"derivedFrom":sQuery(id+"F6.wireOp",EDGE,"E16.1.0.2")}),1.0]])]});
            var Q47;
            Q47=makeQuery(id+"F6.imprint","IMPRINT",FACE,{"disambiguationData":[TD([[makeQuery(id+"F6.imprint","IMPRINT",EDGE,{"derivedFrom":sQuery(id+"F6.wireOp",EDGE,"E16.1.0.5")}),-1.0]])]});
            var Q48;
            {var subQ0=sQuery(id+"F6.wireOp",EDGE,"E16.4.0.23");var subQ1=sQuery(id+"F6.wireOp",EDGE,"E15.top");var subQ2=makeQuery(id+"F6.imprint","INTERSECT",VERTEX,{"derivedFrom":[subQ1,subQ0]});Q48=makeQuery(id+"F6.imprint","IMPRINT",FACE,{"disambiguationData":[TD([[makeQuery(id+"F6.imprint","IMPRINT",EDGE,{"disambiguationData":[TD([[subQ2,-1.0]])],"derivedFrom":subQ1}),1.0]])]});}
            var Q49;
            {var subQ0=sQuery(id+"F6.wireOp",EDGE,"E16.4.0.49");var subQ1=sQuery(id+"F6.wireOp",EDGE,"E15.top");var subQ2=makeQuery(id+"F6.imprint","INTERSECT",VERTEX,{"derivedFrom":[subQ1,subQ0]});Q49=makeQuery(id+"F6.imprint","IMPRINT",FACE,{"disambiguationData":[TD([[makeQuery(id+"F6.imprint","IMPRINT",EDGE,{"disambiguationData":[TD([[subQ2,-1.0]])],"derivedFrom":subQ1}),1.0]])]});}
            var Q50;
            {var subQ0=sQuery(id+"F6.wireOp",EDGE,"E16.4.0.19");var subQ1=sQuery(id+"F6.wireOp",EDGE,"E15.top");var subQ2=makeQuery(id+"F6.imprint","INTERSECT",VERTEX,{"derivedFrom":[subQ1,subQ0]});Q50=makeQuery(id+"F6.imprint","IMPRINT",FACE,{"disambiguationData":[TD([[makeQuery(id+"F6.imprint","IMPRINT",EDGE,{"disambiguationData":[TD([[subQ2,-1.0]])],"derivedFrom":subQ1}),1.0]])]});}
            extrude(context, id + "F7", {"entities" : qUnion([Q0, Q1, Q2, Q3, Q4, Q5, Q6, Q7, Q8, Q9, Q10, Q11, Q12, Q13, Q14, Q15, Q16, Q17, Q18, Q19, Q20, Q21, Q22, Q23, Q24, Q25, Q26, Q27, Q28, Q29, Q30, Q31, Q32, Q33, Q34, Q35, Q36, Q37, Q38, Q39, Q40, Q41, Q42, Q43, Q44, Q45, Q46, Q47, Q48, Q49, Q50]), "operationType" : NewBodyOperationType.REMOVE, "oppositeDirection" : true, "depth" : 25 * mm, "offsetDistance" : 25 * mm});
        }
        {
            var Q0;
            Q0=qCreatedBy(makeId("Right.planeOp"),FACE);
            var sketch = newSketch(context, id + "F8", { "sketchPlane" : qUnion([Q0])});
            skCircle(sketch, "E17", {"center": v(51, 7.02) * mm, "radius": 5 * mm});
            skSolve(sketch);
        }
        {
            var Q0;
            Q0=sQuery(id+"F8.wireOp",VERTEX,"E17.center");
            var Q1;
            Q1=makeQuery(id+"F1.opExtrude","SWEPT_BODY",BODY,{"disambiguationData":[OSD([sQuery(id+"F0.wireOp",EDGE,"E0"),sQuery(id+"F0.wireOp",EDGE,"E1"),sQuery(id+"F0.wireOp",EDGE,"E2"),sQuery(id+"F0.wireOp",EDGE,"E3"),sQuery(id+"F0.wireOp",EDGE,"E4"),sQuery(id+"F0.wireOp",EDGE,"E5"),sQuery(id+"F0.wireOp",EDGE,"E6"),sQuery(id+"F0.wireOp",EDGE,"E7")])]});
            hole(context, id + "F9", {"style" : HoleStyle.SIMPLE, "endStyle" : HoleEndStyle.THROUGH, "standardTappedOrClearance" : lookupTablePath({ "standard" : "ISO", "fit" : "Normal", "size" : "M10", "type" : "Clearance" }), "standardBlindInLast" : lookupTablePath({ "fit" : "Standard", "standard" : "ISO", "size" : "M10", "type" : "Clearance" }), "holeDiameter" : 11 * mm, "majorDiameter" : 5 * mm, "isTappedThrough" : true, "tappedDepth" : 12 * mm, "tapClearance" : 3, "locations" : qUnion([Q0]), "scope" : qUnion([Q1])});
        }
        {
            var Q0;
            Q0=qCreatedBy(makeId("Front.planeOp"),FACE);
            var sketch = newSketch(context, id + "F10", { "sketchPlane" : qUnion([Q0])});
            skCircle(sketch, "E18.cCircle", {"center": v(-6.03, 155.43) * mm, "radius": 5 * mm, "construction": true});
            skLineSegment(sketch, "E18.0", {"start": v(-1.03, 152.54) * mm, "end": v(-6.03, 149.65) * mm});
            skLineSegment(sketch, "E18.1", {"start": v(-6.03, 149.65) * mm, "end": v(-11.03, 152.54) * mm});
            skLineSegment(sketch, "E18.2", {"start": v(-11.03, 152.54) * mm, "end": v(-11.03, 158.31) * mm});
            skLineSegment(sketch, "E18.3", {"start": v(-11.03, 158.31) * mm, "end": v(-6.03, 161.2) * mm});
            skLineSegment(sketch, "E18.4", {"start": v(-6.03, 161.2) * mm, "end": v(-1.03, 158.31) * mm});
            skLineSegment(sketch, "E18.5", {"start": v(-1.03, 158.31) * mm, "end": v(-1.03, 152.54) * mm});
            skPoint(sketch, "E18.0.midPoint", {"position": v(-3.53, 151.1) * mm});
            skPoint(sketch, "E19.1.0.0", {"position": v(21.47, 151.1) * mm});
            skCircle(sketch, "E19.1.0.1", {"center": v(18.97, 155.43) * mm, "radius": 5 * mm, "construction": true});
            skLineSegment(sketch, "E19.1.0.2", {"start": v(18.97, 149.65) * mm, "end": v(13.97, 152.54) * mm});
            skLineSegment(sketch, "E19.1.0.3", {"start": v(18.97, 161.2) * mm, "end": v(23.97, 158.31) * mm});
            skLineSegment(sketch, "E19.1.0.4", {"start": v(13.97, 158.31) * mm, "end": v(18.97, 161.2) * mm});
            skLineSegment(sketch, "E19.1.0.5", {"start": v(23.97, 152.54) * mm, "end": v(18.97, 149.65) * mm});
            skLineSegment(sketch, "E19.1.0.6", {"start": v(23.97, 158.31) * mm, "end": v(23.97, 152.54) * mm});
            skLineSegment(sketch, "E19.1.0.7", {"start": v(13.97, 152.54) * mm, "end": v(13.97, 158.31) * mm});
            skPoint(sketch, "E19.2.0.0", {"position": v(46.47, 151.1) * mm});
            skCircle(sketch, "E19.2.0.1", {"center": v(43.97, 155.43) * mm, "radius": 5 * mm, "construction": true});
            skLineSegment(sketch, "E19.2.0.2", {"start": v(43.97, 149.65) * mm, "end": v(38.97, 152.54) * mm});
            skLineSegment(sketch, "E19.2.0.3", {"start": v(43.97, 161.2) * mm, "end": v(48.97, 158.31) * mm});
            skLineSegment(sketch, "E19.2.0.4", {"start": v(38.97, 158.31) * mm, "end": v(43.97, 161.2) * mm});
            skLineSegment(sketch, "E19.2.0.5", {"start": v(48.97, 152.54) * mm, "end": v(43.97, 149.65) * mm});
            skLineSegment(sketch, "E19.2.0.6", {"start": v(48.97, 158.31) * mm, "end": v(48.97, 152.54) * mm});
            skLineSegment(sketch, "E19.2.0.7", {"start": v(38.97, 152.54) * mm, "end": v(38.97, 158.31) * mm});
            skLineSegment(sketch, "E19.direction1", {"start": v(-11.03, 152.54) * mm, "end": v(13.97, 152.54) * mm, "construction": true});
            skLineSegment(sketch, "E20.1.0.0", {"start": v(49.1, 131.79) * mm, "end": v(49.1, 126.01) * mm});
            skPoint(sketch, "E20.1.0.1", {"position": v(46.6, 124.57) * mm});
            skLineSegment(sketch, "E20.1.0.2", {"start": v(39.1, 126.01) * mm, "end": v(39.1, 131.79) * mm});
            skLineSegment(sketch, "E20.1.0.3", {"start": v(24.1, 131.79) * mm, "end": v(24.1, 126.01) * mm});
            skLineSegment(sketch, "E20.1.0.4", {"start": v(19.1, 134.67) * mm, "end": v(24.1, 131.79) * mm});
            skLineSegment(sketch, "E20.1.0.5", {"start": v(44.1, 134.67) * mm, "end": v(49.1, 131.79) * mm});
            skPoint(sketch, "E20.1.0.6", {"position": v(-3.4, 124.57) * mm});
            skLineSegment(sketch, "E20.1.0.7", {"start": v(-10.9, 126.01) * mm, "end": v(14.1, 126.01) * mm, "construction": true});
            skLineSegment(sketch, "E20.1.0.8", {"start": v(-5.9, 123.13) * mm, "end": v(-10.9, 126.01) * mm});
            skCircle(sketch, "E20.1.0.9", {"center": v(-5.9, 128.9) * mm, "radius": 5 * mm, "construction": true});
            skCircle(sketch, "E20.1.0.10", {"center": v(44.1, 128.9) * mm, "radius": 5 * mm, "construction": true});
            skLineSegment(sketch, "E20.1.0.11", {"start": v(44.1, 123.13) * mm, "end": v(39.1, 126.01) * mm});
            skCircle(sketch, "E20.1.0.12", {"center": v(19.1, 128.9) * mm, "radius": 5 * mm, "construction": true});
            skLineSegment(sketch, "E20.1.0.13", {"start": v(19.1, 123.13) * mm, "end": v(14.1, 126.01) * mm});
            skLineSegment(sketch, "E20.1.0.14", {"start": v(-0.9, 131.79) * mm, "end": v(-0.9, 126.01) * mm});
            skLineSegment(sketch, "E20.1.0.15", {"start": v(-10.9, 126.01) * mm, "end": v(-10.9, 131.79) * mm});
            skLineSegment(sketch, "E20.1.0.16", {"start": v(-10.9, 131.79) * mm, "end": v(-5.9, 134.67) * mm});
            skPoint(sketch, "E20.1.0.17", {"position": v(21.6, 124.57) * mm});
            skLineSegment(sketch, "E20.1.0.18", {"start": v(39.1, 131.79) * mm, "end": v(44.1, 134.67) * mm});
            skLineSegment(sketch, "E20.1.0.19", {"start": v(24.1, 126.01) * mm, "end": v(19.1, 123.13) * mm});
            skLineSegment(sketch, "E20.1.0.20", {"start": v(14.1, 131.79) * mm, "end": v(19.1, 134.67) * mm});
            skLineSegment(sketch, "E20.1.0.21", {"start": v(-0.9, 126.01) * mm, "end": v(-5.9, 123.13) * mm});
            skLineSegment(sketch, "E20.1.0.22", {"start": v(14.1, 126.01) * mm, "end": v(14.1, 131.79) * mm});
            skLineSegment(sketch, "E20.1.0.23", {"start": v(-5.9, 134.67) * mm, "end": v(-0.9, 131.79) * mm});
            skLineSegment(sketch, "E20.1.0.24", {"start": v(49.1, 126.01) * mm, "end": v(44.1, 123.13) * mm});
            skLineSegment(sketch, "E20.2.0.0", {"start": v(49.23, 105.26) * mm, "end": v(49.23, 99.49) * mm});
            skPoint(sketch, "E20.2.0.1", {"position": v(46.73, 98.04) * mm});
            skLineSegment(sketch, "E20.2.0.2", {"start": v(39.23, 99.49) * mm, "end": v(39.23, 105.26) * mm});
            skLineSegment(sketch, "E20.2.0.3", {"start": v(24.23, 105.26) * mm, "end": v(24.23, 99.49) * mm});
            skLineSegment(sketch, "E20.2.0.4", {"start": v(19.23, 108.15) * mm, "end": v(24.23, 105.26) * mm});
            skLineSegment(sketch, "E20.2.0.5", {"start": v(44.23, 108.15) * mm, "end": v(49.23, 105.26) * mm});
            skPoint(sketch, "E20.2.0.6", {"position": v(-3.27, 98.04) * mm});
            skLineSegment(sketch, "E20.2.0.7", {"start": v(-10.77, 99.49) * mm, "end": v(14.23, 99.49) * mm, "construction": true});
            skLineSegment(sketch, "E20.2.0.8", {"start": v(-5.77, 96.6) * mm, "end": v(-10.77, 99.49) * mm});
            skCircle(sketch, "E20.2.0.9", {"center": v(-5.77, 102.37) * mm, "radius": 5 * mm, "construction": true});
            skCircle(sketch, "E20.2.0.10", {"center": v(44.23, 102.37) * mm, "radius": 5 * mm, "construction": true});
            skLineSegment(sketch, "E20.2.0.11", {"start": v(44.23, 96.6) * mm, "end": v(39.23, 99.49) * mm});
            skCircle(sketch, "E20.2.0.12", {"center": v(19.23, 102.37) * mm, "radius": 5 * mm, "construction": true});
            skLineSegment(sketch, "E20.2.0.13", {"start": v(19.23, 96.6) * mm, "end": v(14.23, 99.49) * mm});
            skLineSegment(sketch, "E20.2.0.14", {"start": v(-0.77, 105.26) * mm, "end": v(-0.77, 99.49) * mm});
            skLineSegment(sketch, "E20.2.0.15", {"start": v(-10.77, 99.49) * mm, "end": v(-10.77, 105.26) * mm});
            skLineSegment(sketch, "E20.2.0.16", {"start": v(-10.77, 105.26) * mm, "end": v(-5.77, 108.15) * mm});
            skPoint(sketch, "E20.2.0.17", {"position": v(21.73, 98.04) * mm});
            skLineSegment(sketch, "E20.2.0.18", {"start": v(39.23, 105.26) * mm, "end": v(44.23, 108.15) * mm});
            skLineSegment(sketch, "E20.2.0.19", {"start": v(24.23, 99.49) * mm, "end": v(19.23, 96.6) * mm});
            skLineSegment(sketch, "E20.2.0.20", {"start": v(14.23, 105.26) * mm, "end": v(19.23, 108.15) * mm});
            skLineSegment(sketch, "E20.2.0.21", {"start": v(-0.77, 99.49) * mm, "end": v(-5.77, 96.6) * mm});
            skLineSegment(sketch, "E20.2.0.22", {"start": v(14.23, 99.49) * mm, "end": v(14.23, 105.26) * mm});
            skLineSegment(sketch, "E20.2.0.23", {"start": v(-5.77, 108.15) * mm, "end": v(-0.77, 105.26) * mm});
            skLineSegment(sketch, "E20.2.0.24", {"start": v(49.23, 99.49) * mm, "end": v(44.23, 96.6) * mm});
            skLineSegment(sketch, "E20.3.0.0", {"start": v(49.36, 78.73) * mm, "end": v(49.36, 72.96) * mm});
            skPoint(sketch, "E20.3.0.1", {"position": v(46.86, 71.52) * mm});
            skLineSegment(sketch, "E20.3.0.2", {"start": v(39.36, 72.96) * mm, "end": v(39.36, 78.73) * mm});
            skLineSegment(sketch, "E20.3.0.3", {"start": v(24.36, 78.73) * mm, "end": v(24.36, 72.96) * mm});
            skLineSegment(sketch, "E20.3.0.4", {"start": v(19.36, 81.62) * mm, "end": v(24.36, 78.73) * mm});
            skLineSegment(sketch, "E20.3.0.5", {"start": v(44.36, 81.62) * mm, "end": v(49.36, 78.73) * mm});
            skPoint(sketch, "E20.3.0.6", {"position": v(-3.14, 71.52) * mm});
            skLineSegment(sketch, "E20.3.0.7", {"start": v(-10.64, 72.96) * mm, "end": v(14.36, 72.96) * mm, "construction": true});
            skLineSegment(sketch, "E20.3.0.8", {"start": v(-5.64, 70.07) * mm, "end": v(-10.64, 72.96) * mm});
            skCircle(sketch, "E20.3.0.9", {"center": v(-5.64, 75.85) * mm, "radius": 5 * mm, "construction": true});
            skCircle(sketch, "E20.3.0.10", {"center": v(44.36, 75.85) * mm, "radius": 5 * mm, "construction": true});
            skLineSegment(sketch, "E20.3.0.11", {"start": v(44.36, 70.07) * mm, "end": v(39.36, 72.96) * mm});
            skCircle(sketch, "E20.3.0.12", {"center": v(19.36, 75.85) * mm, "radius": 5 * mm, "construction": true});
            skLineSegment(sketch, "E20.3.0.13", {"start": v(19.36, 70.07) * mm, "end": v(14.36, 72.96) * mm});
            skLineSegment(sketch, "E20.3.0.14", {"start": v(-0.64, 78.73) * mm, "end": v(-0.64, 72.96) * mm});
            skLineSegment(sketch, "E20.3.0.15", {"start": v(-10.64, 72.96) * mm, "end": v(-10.64, 78.73) * mm});
            skLineSegment(sketch, "E20.3.0.16", {"start": v(-10.64, 78.73) * mm, "end": v(-5.64, 81.62) * mm});
            skPoint(sketch, "E20.3.0.17", {"position": v(21.86, 71.52) * mm});
            skLineSegment(sketch, "E20.3.0.18", {"start": v(39.36, 78.73) * mm, "end": v(44.36, 81.62) * mm});
            skLineSegment(sketch, "E20.3.0.19", {"start": v(24.36, 72.96) * mm, "end": v(19.36, 70.07) * mm});
            skLineSegment(sketch, "E20.3.0.20", {"start": v(14.36, 78.73) * mm, "end": v(19.36, 81.62) * mm});
            skLineSegment(sketch, "E20.3.0.21", {"start": v(-0.64, 72.96) * mm, "end": v(-5.64, 70.07) * mm});
            skLineSegment(sketch, "E20.3.0.22", {"start": v(14.36, 72.96) * mm, "end": v(14.36, 78.73) * mm});
            skLineSegment(sketch, "E20.3.0.23", {"start": v(-5.64, 81.62) * mm, "end": v(-0.64, 78.73) * mm});
            skLineSegment(sketch, "E20.3.0.24", {"start": v(49.36, 72.96) * mm, "end": v(44.36, 70.07) * mm});
            skLineSegment(sketch, "E20.direction1", {"start": v(-11.03, 152.54) * mm, "end": v(-10.9, 126.01) * mm, "construction": true});
            skSolve(sketch);
        }
        {
            var Q0;
            Q0 = qSketchRegion(id + "F10", true);
            extrude(context, id + "F11", {"entities" : qUnion([Q0]), "operationType" : NewBodyOperationType.REMOVE, "oppositeDirection" : true, "depth" : 25 * mm, "offsetDistance" : 25 * mm});
        }
        {
            var Q0;
            Q0=qCreatedBy(makeId("Front.planeOp"),FACE);
            var sketch = newSketch(context, id + "F12", { "sketchPlane" : qUnion([Q0])});
            skLineSegment(sketch, "E21.bottom", {"start": v(-33.7, 155.83) * mm, "end": v(71.3, 155.83) * mm});
            skLineSegment(sketch, "E21.top", {"start": v(-33.7, 50.83) * mm, "end": v(71.3, 50.83) * mm});
            skLineSegment(sketch, "E21.left", {"start": v(-33.7, 155.83) * mm, "end": v(-33.7, 50.83) * mm});
            skLineSegment(sketch, "E21.right", {"start": v(71.3, 155.83) * mm, "end": v(71.3, 50.83) * mm});
            skCircle(sketch, "E22", {"center": v(-33.7, 155.83) * mm, "radius": 2.24 * mm});
            skCircle(sketch, "E23", {"center": v(71.3, 155.83) * mm, "radius": 2.24 * mm});
            skCircle(sketch, "E24", {"center": v(71.3, 50.83) * mm, "radius": 2.2 * mm});
            skCircle(sketch, "E25", {"center": v(-33.7, 50.83) * mm, "radius": 2.27 * mm});
            skSolve(sketch);
        }
        {
            var Q0;
            Q0=sQuery(id+"F12.wireOp",VERTEX,"E21.bottom.start");
            var Q1;
            Q1=sQuery(id+"F12.wireOp",VERTEX,"E21.bottom.end");
            var Q2;
            Q2=sQuery(id+"F12.wireOp",VERTEX,"E21.top.end");
            var Q3;
            Q3=sQuery(id+"F12.wireOp",VERTEX,"E21.top.start");
            var Q4;
            Q4=makeQuery(id+"F1.opExtrude","SWEPT_BODY",BODY,{"disambiguationData":[OSD([sQuery(id+"F0.wireOp",EDGE,"E0"),sQuery(id+"F0.wireOp",EDGE,"E1"),sQuery(id+"F0.wireOp",EDGE,"E2"),sQuery(id+"F0.wireOp",EDGE,"E3"),sQuery(id+"F0.wireOp",EDGE,"E4"),sQuery(id+"F0.wireOp",EDGE,"E5"),sQuery(id+"F0.wireOp",EDGE,"E6"),sQuery(id+"F0.wireOp",EDGE,"E7")])]});
            hole(context, id + "F13", {"style" : HoleStyle.SIMPLE, "endStyle" : HoleEndStyle.THROUGH, "standardTappedOrClearance" : lookupTablePath({ "standard" : "ISO", "fit" : "Normal", "size" : "M4", "type" : "Clearance" }), "standardBlindInLast" : lookupTablePath({ "fit" : "Standard", "standard" : "ISO", "size" : "M4", "type" : "Clearance" }), "holeDiameter" : 4.4 * mm, "majorDiameter" : 5 * mm, "isTappedThrough" : true, "tappedDepth" : 12 * mm, "tapClearance" : 3, "locations" : qUnion([Q0, Q1, Q2, Q3]), "scope" : qUnion([Q4])});
        }
        {
            var Q0;
            Q0=qCreatedBy(makeId("Right.planeOp"),FACE);
            var sketch = newSketch(context, id + "F14", { "sketchPlane" : qUnion([Q0])});
            skLineSegment(sketch, "E26.0.2.0", {"start": v(17.58, 86.22) * mm, "end": v(32.58, 86.22) * mm});
            skLineSegment(sketch, "E26.0.2.1", {"start": v(17.58, 90.7) * mm, "end": v(32.58, 90.7) * mm});
            skPoint(sketch, "E26.0.2.2", {"position": v(25, 87.94) * mm});
            skPoint(sketch, "E26.0.2.3", {"position": v(25.08, 90.7) * mm});
            skLineSegment(sketch, "E26.0.2.4", {"start": v(17.58, 87.47) * mm, "end": v(32.58, 87.47) * mm});
            skLineSegment(sketch, "E26.0.2.5", {"start": v(17.58, 89.46) * mm, "end": v(32.58, 89.46) * mm});
            skLineSegment(sketch, "E26.0.2.6", {"start": v(17.58, 87.47) * mm, "end": v(32.58, 87.47) * mm});
            skLineSegment(sketch, "E26.0.2.7", {"start": v(32.58, 86.22) * mm, "end": v(32.58, 87.47) * mm});
            skLineSegment(sketch, "E26.0.2.8", {"start": v(17.58, 86.22) * mm, "end": v(17.58, 87.47) * mm});
            skLineSegment(sketch, "E26.0.2.9", {"start": v(17.58, 90.7) * mm, "end": v(17.58, 89.46) * mm});
            skLineSegment(sketch, "E26.0.2.10", {"start": v(32.58, 90.7) * mm, "end": v(32.58, 89.46) * mm});
            skLineSegment(sketch, "E26.0.3.0", {"start": v(17.58, 111.22) * mm, "end": v(32.58, 111.22) * mm});
            skLineSegment(sketch, "E26.0.3.1", {"start": v(17.58, 115.7) * mm, "end": v(32.58, 115.7) * mm});
            skPoint(sketch, "E26.0.3.2", {"position": v(25, 112.94) * mm});
            skPoint(sketch, "E26.0.3.3", {"position": v(25.08, 115.7) * mm});
            skLineSegment(sketch, "E26.0.3.4", {"start": v(17.58, 112.47) * mm, "end": v(32.58, 112.47) * mm});
            skLineSegment(sketch, "E26.0.3.5", {"start": v(17.58, 114.46) * mm, "end": v(32.58, 114.46) * mm});
            skLineSegment(sketch, "E26.0.3.6", {"start": v(17.58, 112.47) * mm, "end": v(32.58, 112.47) * mm});
            skLineSegment(sketch, "E26.0.3.7", {"start": v(32.58, 111.22) * mm, "end": v(32.58, 112.47) * mm});
            skLineSegment(sketch, "E26.0.3.8", {"start": v(17.58, 111.22) * mm, "end": v(17.58, 112.47) * mm});
            skLineSegment(sketch, "E26.0.3.9", {"start": v(17.58, 115.7) * mm, "end": v(17.58, 114.46) * mm});
            skLineSegment(sketch, "E26.0.3.10", {"start": v(32.58, 115.7) * mm, "end": v(32.58, 114.46) * mm});
            skLineSegment(sketch, "E26.0.4.0", {"start": v(17.58, 136.22) * mm, "end": v(32.58, 136.22) * mm});
            skLineSegment(sketch, "E26.0.4.1", {"start": v(17.58, 140.7) * mm, "end": v(32.58, 140.7) * mm});
            skPoint(sketch, "E26.0.4.2", {"position": v(25, 137.94) * mm});
            skPoint(sketch, "E26.0.4.3", {"position": v(25.08, 140.7) * mm});
            skLineSegment(sketch, "E26.0.4.4", {"start": v(17.58, 137.47) * mm, "end": v(32.58, 137.47) * mm});
            skLineSegment(sketch, "E26.0.4.5", {"start": v(17.58, 139.46) * mm, "end": v(32.58, 139.46) * mm});
            skLineSegment(sketch, "E26.0.4.6", {"start": v(17.58, 137.47) * mm, "end": v(32.58, 137.47) * mm});
            skLineSegment(sketch, "E26.0.4.7", {"start": v(32.58, 136.22) * mm, "end": v(32.58, 137.47) * mm});
            skLineSegment(sketch, "E26.0.4.8", {"start": v(17.58, 136.22) * mm, "end": v(17.58, 137.47) * mm});
            skLineSegment(sketch, "E26.0.4.9", {"start": v(17.58, 140.7) * mm, "end": v(17.58, 139.46) * mm});
            skLineSegment(sketch, "E26.0.4.10", {"start": v(32.58, 140.7) * mm, "end": v(32.58, 139.46) * mm});
            skLineSegment(sketch, "E26.0.5.0", {"start": v(17.58, 161.22) * mm, "end": v(32.58, 161.22) * mm});
            skLineSegment(sketch, "E26.0.5.1", {"start": v(17.58, 165.7) * mm, "end": v(32.58, 165.7) * mm});
            skPoint(sketch, "E26.0.5.2", {"position": v(25, 162.94) * mm});
            skPoint(sketch, "E26.0.5.3", {"position": v(25.08, 165.7) * mm});
            skLineSegment(sketch, "E26.0.5.4", {"start": v(17.58, 162.47) * mm, "end": v(32.58, 162.47) * mm});
            skLineSegment(sketch, "E26.0.5.5", {"start": v(17.58, 164.46) * mm, "end": v(32.58, 164.46) * mm});
            skLineSegment(sketch, "E26.0.5.6", {"start": v(17.58, 162.47) * mm, "end": v(32.58, 162.47) * mm});
            skLineSegment(sketch, "E26.0.5.7", {"start": v(32.58, 161.22) * mm, "end": v(32.58, 162.47) * mm});
            skLineSegment(sketch, "E26.0.5.8", {"start": v(17.58, 161.22) * mm, "end": v(17.58, 162.47) * mm});
            skLineSegment(sketch, "E26.0.5.9", {"start": v(17.58, 165.7) * mm, "end": v(17.58, 164.46) * mm});
            skLineSegment(sketch, "E26.0.5.10", {"start": v(32.58, 165.7) * mm, "end": v(32.58, 164.46) * mm});
            skSolve(sketch);
        }
        {
            var Q0;
            Q0 = qSketchRegion(id + "F14", true);
            extrude(context, id + "F15", {"entities" : qUnion([Q0]), "operationType" : NewBodyOperationType.REMOVE, "oppositeDirection" : true, "depth" : 51 * mm, "offsetDistance" : 25 * mm});
        }
        {
            var Q0;
            Q0=qCreatedBy(makeId("Right.planeOp"),FACE);
            var sketch = newSketch(context, id + "F16", { "sketchPlane" : qUnion([Q0])});
            skLineSegment(sketch, "E27.bottom", {"start": v(26, 17.44) * mm, "end": v(28.5, 17.44) * mm});
            skLineSegment(sketch, "E27.top", {"start": v(26, 67.44) * mm, "end": v(28.5, 67.44) * mm});
            skLineSegment(sketch, "E27.left", {"start": v(26, 17.44) * mm, "end": v(26, 67.44) * mm});
            skLineSegment(sketch, "E27.right", {"start": v(28.5, 17.44) * mm, "end": v(28.5, 67.44) * mm});
            skSolve(sketch);
        }
        {
            var Q0;
            Q0 = qSketchRegion(id + "F16", true);
            extrude(context, id + "F17", {"entities" : qUnion([Q0]), "operationType" : NewBodyOperationType.REMOVE, "oppositeDirection" : true, "depth" : -80 * mm, "offsetDistance" : 25 * mm});
        }
    });
